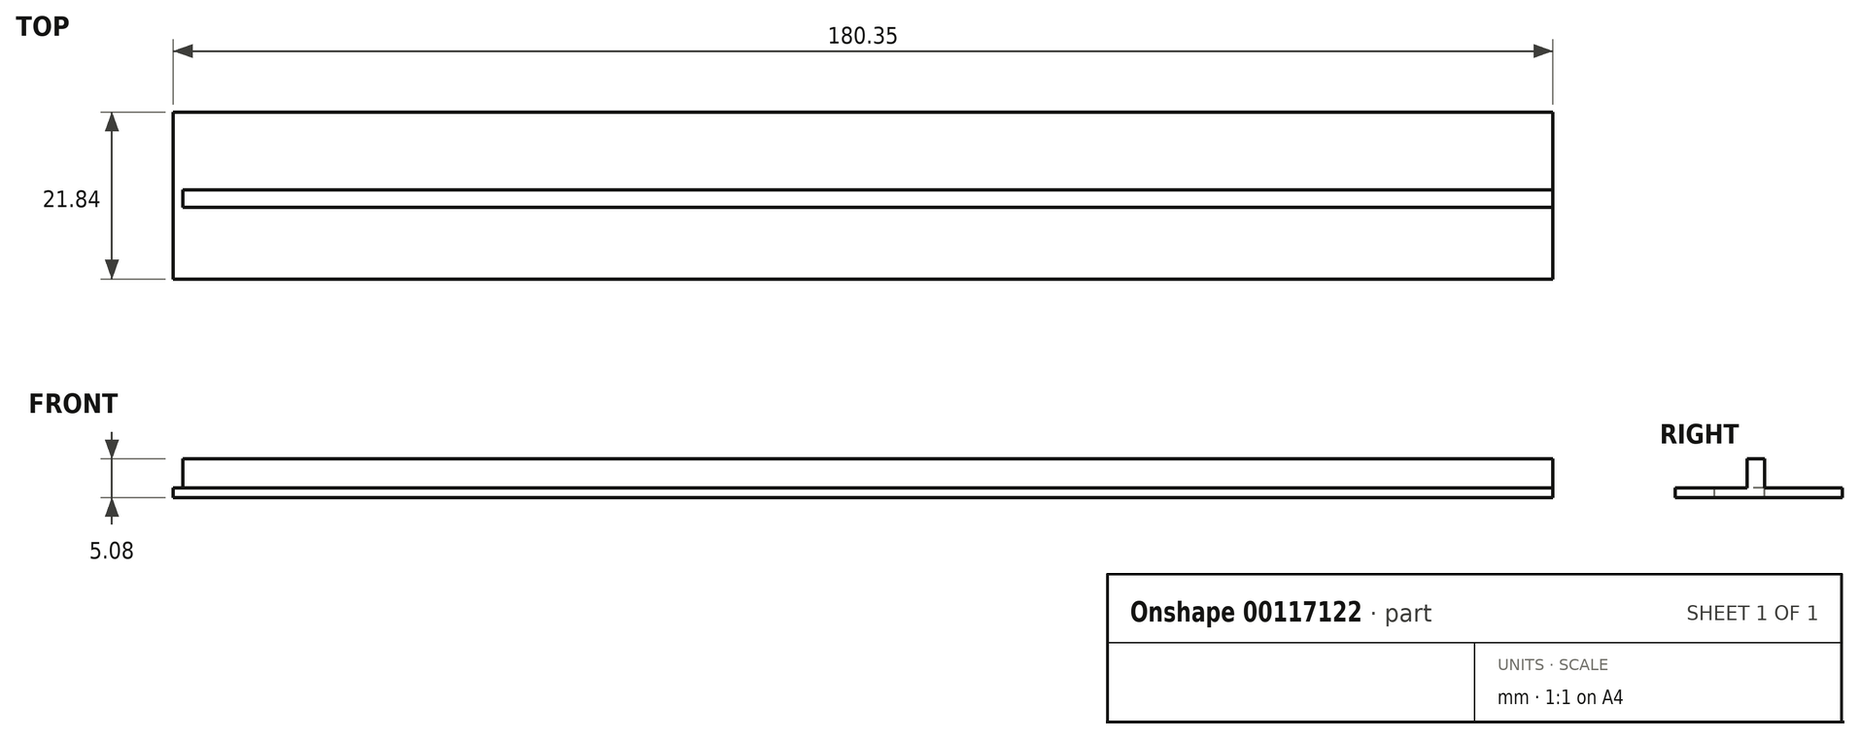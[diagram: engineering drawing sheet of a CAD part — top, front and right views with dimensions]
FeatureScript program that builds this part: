
annotation { "Feature Type Name" : "Feature", "Feature Type Description" : "" }
export const myFeature = defineFeature(function(context is Context, id is Id, definition is map)
    precondition{}
    {
        {
            var Q0;
            Q0=qCreatedBy(makeId("Front.planeOp"),FACE);
            var sketch = newSketch(context, id + "F0", { "sketchPlane" : qUnion([Q0])});
            skLineSegment(sketch, "E0.bottom", {"start": v(107.95, -50.8) * mm, "end": v(-107.95, -50.8) * mm});
            skLineSegment(sketch, "E0.top", {"start": v(107.95, 50.8) * mm, "end": v(-107.95, 50.8) * mm});
            skLineSegment(sketch, "E0.left", {"start": v(107.95, -50.8) * mm, "end": v(107.95, 50.8) * mm});
            skLineSegment(sketch, "E0.right", {"start": v(-107.95, -50.8) * mm, "end": v(-107.95, 50.8) * mm});
            skPoint(sketch, "E0.middle", {"position": v(0, 0) * mm});
            skLineSegment(sketch, "E1.bottom", {"start": v(88.9, -31.75) * mm, "end": v(-88.9, -31.75) * mm});
            skLineSegment(sketch, "E1.top", {"start": v(88.9, 31.75) * mm, "end": v(-88.9, 31.75) * mm});
            skLineSegment(sketch, "E1.left", {"start": v(88.9, -31.75) * mm, "end": v(88.9, 31.75) * mm});
            skLineSegment(sketch, "E1.right", {"start": v(-88.9, -31.75) * mm, "end": v(-88.9, 31.75) * mm});
            skSolve(sketch);
        }
        {
            var Q0;
            Q0=makeQuery(id+"F0.imprint","IMPRINT",FACE,{"disambiguationData":[TD([[makeQuery(id+"F0.imprint","IMPRINT",EDGE,{"derivedFrom":sQuery(id+"F0.wireOp",EDGE,"E0.bottom")}),-1.0]])]});
            extrude(context, id + "F1", {"entities" : qUnion([Q0]), "depth" : 12.7 * mm});
        }
        {
            var Q0;
            Q0=makeQuery(id+"F1.opExtrude","SWEPT_FACE",FACE,{"disambiguationData":[OSD([sQuery(id+"F0.wireOp",EDGE,"E0.top")])]});
            var sketch = newSketch(context, id + "F2", { "sketchPlane" : qUnion([Q0])});
            skLineSegment(sketch, "E2", {"start": v(-75.05, 0) * mm, "end": v(-80.97, -12.7) * mm});
            skLineSegment(sketch, "E3", {"start": v(-80.97, -12.7) * mm, "end": v(-78.17, -12.7) * mm});
            skLineSegment(sketch, "E4", {"start": v(-78.17, -12.7) * mm, "end": v(-72.25, 0) * mm});
            skLineSegment(sketch, "E5", {"start": v(-72.25, 0) * mm, "end": v(-75.05, 0) * mm});
            skLineSegment(sketch, "E6.1.0.0", {"start": v(-64.33, 0) * mm, "end": v(-70.25, -12.7) * mm});
            skLineSegment(sketch, "E6.1.0.1", {"start": v(-70.25, -12.7) * mm, "end": v(-67.45, -12.7) * mm});
            skLineSegment(sketch, "E6.1.0.2", {"start": v(-67.45, -12.7) * mm, "end": v(-61.53, 0) * mm});
            skLineSegment(sketch, "E6.1.0.3", {"start": v(-61.53, 0) * mm, "end": v(-64.33, 0) * mm});
            skLineSegment(sketch, "E6.2.0.0", {"start": v(-53.6, 0) * mm, "end": v(-59.53, -12.7) * mm});
            skLineSegment(sketch, "E6.2.0.1", {"start": v(-59.53, -12.7) * mm, "end": v(-56.73, -12.7) * mm});
            skLineSegment(sketch, "E6.2.0.2", {"start": v(-56.73, -12.7) * mm, "end": v(-50.8, 0) * mm});
            skLineSegment(sketch, "E6.2.0.3", {"start": v(-50.8, 0) * mm, "end": v(-53.6, 0) * mm});
            skLineSegment(sketch, "E6.3.0.0", {"start": v(-42.88, 0) * mm, "end": v(-48.8, -12.7) * mm});
            skLineSegment(sketch, "E6.3.0.1", {"start": v(-48.8, -12.7) * mm, "end": v(-46, -12.7) * mm});
            skLineSegment(sketch, "E6.3.0.2", {"start": v(-46, -12.7) * mm, "end": v(-40.08, 0) * mm});
            skLineSegment(sketch, "E6.3.0.3", {"start": v(-40.08, 0) * mm, "end": v(-42.88, 0) * mm});
            skLineSegment(sketch, "E6.4.0.0", {"start": v(-32.16, 0) * mm, "end": v(-38.08, -12.7) * mm});
            skLineSegment(sketch, "E6.4.0.1", {"start": v(-38.08, -12.7) * mm, "end": v(-35.28, -12.7) * mm});
            skLineSegment(sketch, "E6.4.0.2", {"start": v(-35.28, -12.7) * mm, "end": v(-29.36, 0) * mm});
            skLineSegment(sketch, "E6.4.0.3", {"start": v(-29.36, 0) * mm, "end": v(-32.16, 0) * mm});
            skLineSegment(sketch, "E6.5.0.0", {"start": v(-21.44, 0) * mm, "end": v(-27.36, -12.7) * mm});
            skLineSegment(sketch, "E6.5.0.1", {"start": v(-27.36, -12.7) * mm, "end": v(-24.56, -12.7) * mm});
            skLineSegment(sketch, "E6.5.0.2", {"start": v(-24.56, -12.7) * mm, "end": v(-18.64, 0) * mm});
            skLineSegment(sketch, "E6.5.0.3", {"start": v(-18.64, 0) * mm, "end": v(-21.44, 0) * mm});
            skLineSegment(sketch, "E6.6.0.0", {"start": v(-10.72, 0) * mm, "end": v(-16.64, -12.7) * mm});
            skLineSegment(sketch, "E6.6.0.1", {"start": v(-16.64, -12.7) * mm, "end": v(-13.84, -12.7) * mm});
            skLineSegment(sketch, "E6.6.0.2", {"start": v(-13.84, -12.7) * mm, "end": v(-7.92, 0) * mm});
            skLineSegment(sketch, "E6.6.0.3", {"start": v(-7.92, 0) * mm, "end": v(-10.72, 0) * mm});
            skLineSegment(sketch, "E6.direction1", {"start": v(-80.97, -12.7) * mm, "end": v(-70.25, -12.7) * mm, "construction": true});
            skLineSegment(sketch, "E7", {"start": v(75.05, 0) * mm, "end": v(80.97, -12.7) * mm});
            skLineSegment(sketch, "E8", {"start": v(80.97, -12.7) * mm, "end": v(78.17, -12.7) * mm});
            skLineSegment(sketch, "E9", {"start": v(78.17, -12.7) * mm, "end": v(72.25, 0) * mm});
            skLineSegment(sketch, "E10", {"start": v(72.25, 0) * mm, "end": v(75.05, 0) * mm});
            skLineSegment(sketch, "E11.1.0.0", {"start": v(70.25, -12.7) * mm, "end": v(67.45, -12.7) * mm});
            skLineSegment(sketch, "E11.1.0.1", {"start": v(64.33, 0) * mm, "end": v(70.25, -12.7) * mm});
            skLineSegment(sketch, "E11.1.0.2", {"start": v(61.53, 0) * mm, "end": v(64.33, 0) * mm});
            skLineSegment(sketch, "E11.1.0.3", {"start": v(67.45, -12.7) * mm, "end": v(61.53, 0) * mm});
            skLineSegment(sketch, "E11.2.0.0", {"start": v(59.53, -12.7) * mm, "end": v(56.73, -12.7) * mm});
            skLineSegment(sketch, "E11.2.0.1", {"start": v(53.6, 0) * mm, "end": v(59.53, -12.7) * mm});
            skLineSegment(sketch, "E11.2.0.2", {"start": v(50.8, 0) * mm, "end": v(53.6, 0) * mm});
            skLineSegment(sketch, "E11.2.0.3", {"start": v(56.73, -12.7) * mm, "end": v(50.8, 0) * mm});
            skLineSegment(sketch, "E11.3.0.0", {"start": v(48.8, -12.7) * mm, "end": v(46, -12.7) * mm});
            skLineSegment(sketch, "E11.3.0.1", {"start": v(42.88, 0) * mm, "end": v(48.8, -12.7) * mm});
            skLineSegment(sketch, "E11.3.0.2", {"start": v(40.08, 0) * mm, "end": v(42.88, 0) * mm});
            skLineSegment(sketch, "E11.3.0.3", {"start": v(46, -12.7) * mm, "end": v(40.08, 0) * mm});
            skLineSegment(sketch, "E11.4.0.0", {"start": v(38.08, -12.7) * mm, "end": v(35.28, -12.7) * mm});
            skLineSegment(sketch, "E11.4.0.1", {"start": v(32.16, 0) * mm, "end": v(38.08, -12.7) * mm});
            skLineSegment(sketch, "E11.4.0.2", {"start": v(29.36, 0) * mm, "end": v(32.16, 0) * mm});
            skLineSegment(sketch, "E11.4.0.3", {"start": v(35.28, -12.7) * mm, "end": v(29.36, 0) * mm});
            skLineSegment(sketch, "E11.5.0.0", {"start": v(27.36, -12.7) * mm, "end": v(24.56, -12.7) * mm});
            skLineSegment(sketch, "E11.5.0.1", {"start": v(21.44, 0) * mm, "end": v(27.36, -12.7) * mm});
            skLineSegment(sketch, "E11.5.0.2", {"start": v(18.64, 0) * mm, "end": v(21.44, 0) * mm});
            skLineSegment(sketch, "E11.5.0.3", {"start": v(24.56, -12.7) * mm, "end": v(18.64, 0) * mm});
            skLineSegment(sketch, "E11.6.0.0", {"start": v(16.64, -12.7) * mm, "end": v(13.84, -12.7) * mm});
            skLineSegment(sketch, "E11.6.0.1", {"start": v(10.72, 0) * mm, "end": v(16.64, -12.7) * mm});
            skLineSegment(sketch, "E11.6.0.2", {"start": v(7.92, 0) * mm, "end": v(10.72, 0) * mm});
            skLineSegment(sketch, "E11.6.0.3", {"start": v(13.84, -12.7) * mm, "end": v(7.92, 0) * mm});
            skLineSegment(sketch, "E11.direction1", {"start": v(78.17, -12.7) * mm, "end": v(67.45, -12.7) * mm, "construction": true});
            skLineSegment(sketch, "E12", {"start": v(0, 0) * mm, "end": v(0, -12.7) * mm, "construction": true});
            skLineSegment(sketch, "E13", {"start": v(0, 0) * mm, "end": v(-5.92, -12.7) * mm});
            skLineSegment(sketch, "E14", {"start": v(0, 0) * mm, "end": v(5.92, -12.7) * mm});
            skLineSegment(sketch, "E15", {"start": v(-5.92, -12.7) * mm, "end": v(5.92, -12.7) * mm});
            skSolve(sketch);
        }
        {
            var Q0;
            Q0=qSketchRegion(id+"F2",true);
            extrude(context, id + "F3", {"entities" : qUnion([Q0]), "operationType" : NewBodyOperationType.ADD, "oppositeDirection" : true, "depth" : 101.6 * mm});
        }
        {
            var Q0;
            Q0=makeQuery(id+"F1.opExtrude","CAP_EDGE",EDGE,{"disambiguationData":[OSD([sQuery(id+"F0.wireOp",EDGE,"E0.top")])],"isStart":false});
            var Q1;
            Q1=makeQuery(id+"F1.opExtrude","CAP_EDGE",EDGE,{"disambiguationData":[OSD([sQuery(id+"F0.wireOp",EDGE,"E0.right")])],"isStart":false});
            var Q2;
            Q2=makeQuery(id+"F1.opExtrude","CAP_EDGE",EDGE,{"disambiguationData":[OSD([sQuery(id+"F0.wireOp",EDGE,"E0.bottom")])],"isStart":false});
            var Q3;
            Q3=makeQuery(id+"F1.opExtrude","CAP_EDGE",EDGE,{"disambiguationData":[OSD([sQuery(id+"F0.wireOp",EDGE,"E0.left")])],"isStart":false});
            fillet(context, id + "F4", {"entities" : qUnion([Q0, Q1, Q2, Q3]), "radius" : 12.7 * mm, "tangentPropagation" : true, "allowEdgeOverflow" : false});
        }
        {
            var Q0;
            Q0=makeQuery(id+"F3.boolean.opBoolean","MERGE",FACE,{"derivedFrom":[makeQuery(id+"F1.opExtrude","CAP_FACE",FACE,{"disambiguationData":[OSD([sQuery(id+"F0.wireOp",EDGE,"E0.bottom"),sQuery(id+"F0.wireOp",EDGE,"E0.top"),sQuery(id+"F0.wireOp",EDGE,"E0.left"),sQuery(id+"F0.wireOp",EDGE,"E0.right"),sQuery(id+"F0.wireOp",EDGE,"E1.bottom"),sQuery(id+"F0.wireOp",EDGE,"E1.top"),sQuery(id+"F0.wireOp",EDGE,"E1.left"),sQuery(id+"F0.wireOp",EDGE,"E1.right")])],"isStart":true}),makeQuery(id+"F3.opExtrude","SWEPT_FACE",FACE,{"disambiguationData":[OSD([sQuery(id+"F2.wireOp",EDGE,"E5")])]}),makeQuery(id+"F3.opExtrude","SWEPT_FACE",FACE,{"disambiguationData":[OSD([sQuery(id+"F2.wireOp",EDGE,"E6.1.0.3")])]}),makeQuery(id+"F3.opExtrude","SWEPT_FACE",FACE,{"disambiguationData":[OSD([sQuery(id+"F2.wireOp",EDGE,"E6.2.0.3")])]}),makeQuery(id+"F3.opExtrude","SWEPT_FACE",FACE,{"disambiguationData":[OSD([sQuery(id+"F2.wireOp",EDGE,"E6.3.0.3")])]}),makeQuery(id+"F3.opExtrude","SWEPT_FACE",FACE,{"disambiguationData":[OSD([sQuery(id+"F2.wireOp",EDGE,"E6.4.0.3")])]}),makeQuery(id+"F3.opExtrude","SWEPT_FACE",FACE,{"disambiguationData":[OSD([sQuery(id+"F2.wireOp",EDGE,"E6.5.0.3")])]}),makeQuery(id+"F3.opExtrude","SWEPT_FACE",FACE,{"disambiguationData":[OSD([sQuery(id+"F2.wireOp",EDGE,"E6.6.0.3")])]}),makeQuery(id+"F3.opExtrude","SWEPT_FACE",FACE,{"disambiguationData":[OSD([sQuery(id+"F2.wireOp",EDGE,"E10")])]}),makeQuery(id+"F3.opExtrude","SWEPT_FACE",FACE,{"disambiguationData":[OSD([sQuery(id+"F2.wireOp",EDGE,"E11.1.0.2")])]}),makeQuery(id+"F3.opExtrude","SWEPT_FACE",FACE,{"disambiguationData":[OSD([sQuery(id+"F2.wireOp",EDGE,"E11.2.0.2")])]}),makeQuery(id+"F3.opExtrude","SWEPT_FACE",FACE,{"disambiguationData":[OSD([sQuery(id+"F2.wireOp",EDGE,"E11.3.0.2")])]}),makeQuery(id+"F3.opExtrude","SWEPT_FACE",FACE,{"disambiguationData":[OSD([sQuery(id+"F2.wireOp",EDGE,"E11.4.0.2")])]}),makeQuery(id+"F3.opExtrude","SWEPT_FACE",FACE,{"disambiguationData":[OSD([sQuery(id+"F2.wireOp",EDGE,"E11.5.0.2")])]}),makeQuery(id+"F3.opExtrude","SWEPT_FACE",FACE,{"disambiguationData":[OSD([sQuery(id+"F2.wireOp",EDGE,"E11.6.0.2")])]})]});
            var sketch = newSketch(context, id + "F5", { "sketchPlane" : qUnion([Q0])});
            skLineSegment(sketch, "E16.bottom", {"start": v(90.17, -33.02) * mm, "end": v(-90.17, -33.02) * mm});
            skLineSegment(sketch, "E16.top", {"start": v(90.17, 33.02) * mm, "end": v(-90.17, 33.02) * mm});
            skLineSegment(sketch, "E16.right", {"start": v(-90.17, -33.02) * mm, "end": v(-90.17, 33.02) * mm});
            skPoint(sketch, "E16.middle", {"position": v(0, 0) * mm});
            skLineSegment(sketch, "E17.bottom", {"start": v(88.9, -31.75) * mm, "end": v(-88.9, -31.75) * mm});
            skLineSegment(sketch, "E17.top", {"start": v(88.9, 31.75) * mm, "end": v(-88.9, 31.75) * mm});
            skLineSegment(sketch, "E17.right", {"start": v(-88.9, -31.75) * mm, "end": v(-88.9, 31.75) * mm});
            skLineSegment(sketch, "E18", {"start": v(88.9, 31.75) * mm, "end": v(90.17, 31.75) * mm});
            skLineSegment(sketch, "E19", {"start": v(90.17, 31.75) * mm, "end": v(90.17, 33.02) * mm});
            skLineSegment(sketch, "E20", {"start": v(88.9, -31.75) * mm, "end": v(90.17, -31.75) * mm});
            skLineSegment(sketch, "E21", {"start": v(90.17, -31.75) * mm, "end": v(90.17, -33.02) * mm});
            skSolve(sketch);
        }
        {
            var Q0;
            Q0=qSketchRegion(id+"F5",true);
            extrude(context, id + "F6", {"entities" : qUnion([Q0]), "operationType" : NewBodyOperationType.ADD, "depth" : 3.3 * mm});
        }
        {
            var Q0;
            Q0=makeQuery(id+"F6.opExtrude","CAP_FACE",FACE,{"disambiguationData":[OSD([sQuery(id+"F5.wireOp",EDGE,"E16.bottom"),sQuery(id+"F5.wireOp",EDGE,"E16.top"),sQuery(id+"F5.wireOp",EDGE,"E16.right"),sQuery(id+"F5.wireOp",EDGE,"E17.bottom"),sQuery(id+"F5.wireOp",EDGE,"E17.top"),sQuery(id+"F5.wireOp",EDGE,"E17.right"),sQuery(id+"F5.wireOp",EDGE,"E18"),sQuery(id+"F5.wireOp",EDGE,"E19"),sQuery(id+"F5.wireOp",EDGE,"E20"),sQuery(id+"F5.wireOp",EDGE,"E21")])],"isStart":false});
            var sketch = newSketch(context, id + "F7", { "sketchPlane" : qUnion([Q0])});
            skLineSegment(sketch, "E22.bottom", {"start": v(-90.17, 33.02) * mm, "end": v(88.9, 33.02) * mm});
            skLineSegment(sketch, "E22.top", {"start": v(-90.17, -33.02) * mm, "end": v(88.9, -33.02) * mm});
            skLineSegment(sketch, "E22.left", {"start": v(-90.17, 33.02) * mm, "end": v(-90.17, -33.02) * mm});
            skLineSegment(sketch, "E22.right", {"start": v(88.9, 33.02) * mm, "end": v(88.9, -33.02) * mm});
            skLineSegment(sketch, "E23.bottom", {"start": v(-86.36, 27.94) * mm, "end": v(86.36, 27.94) * mm});
            skLineSegment(sketch, "E23.top", {"start": v(-86.36, -27.94) * mm, "end": v(86.36, -27.94) * mm});
            skLineSegment(sketch, "E23.left", {"start": v(-86.36, 27.94) * mm, "end": v(-86.36, -27.94) * mm});
            skLineSegment(sketch, "E23.right", {"start": v(86.36, 27.94) * mm, "end": v(86.36, -27.94) * mm});
            skSolve(sketch);
        }
        {
            var Q0;
            Q0=qSketchRegion(id+"F7",true);
            extrude(context, id + "F8", {"entities" : qUnion([Q0]), "operationType" : NewBodyOperationType.ADD, "depth" : 1.78 * mm});
        }
        {
            var Q0;
            Q0=makeQuery(id+"F8.opExtrude","CAP_FACE",FACE,{"disambiguationData":[OSD([sQuery(id+"F7.wireOp",EDGE,"E22.bottom"),sQuery(id+"F7.wireOp",EDGE,"E22.top"),sQuery(id+"F7.wireOp",EDGE,"E22.left"),sQuery(id+"F7.wireOp",EDGE,"E22.right"),sQuery(id+"F7.wireOp",EDGE,"E23.bottom"),sQuery(id+"F7.wireOp",EDGE,"E23.top"),sQuery(id+"F7.wireOp",EDGE,"E23.left"),sQuery(id+"F7.wireOp",EDGE,"E23.right")])],"isStart":false});
            var sketch = newSketch(context, id + "F9", { "sketchPlane" : qUnion([Q0])});
            skLineSegment(sketch, "E24.bottom", {"start": v(-90.17, 33.02) * mm, "end": v(88.9, 33.02) * mm});
            skLineSegment(sketch, "E24.top", {"start": v(-90.17, -33.02) * mm, "end": v(88.9, -33.02) * mm});
            skLineSegment(sketch, "E24.left", {"start": v(-90.17, 33.02) * mm, "end": v(-90.17, -33.02) * mm});
            skLineSegment(sketch, "E25.bottom", {"start": v(-88.9, 31.75) * mm, "end": v(87.63, 31.75) * mm});
            skLineSegment(sketch, "E25.top", {"start": v(-88.9, -31.75) * mm, "end": v(87.63, -31.75) * mm});
            skLineSegment(sketch, "E25.left", {"start": v(-88.9, 31.75) * mm, "end": v(-88.9, -31.75) * mm});
            skLineSegment(sketch, "E26", {"start": v(88.9, -33.02) * mm, "end": v(90.18, -33.02) * mm});
            skLineSegment(sketch, "E27", {"start": v(90.18, -33.02) * mm, "end": v(90.18, -31.75) * mm});
            skLineSegment(sketch, "E28", {"start": v(90.18, -31.75) * mm, "end": v(87.63, -31.75) * mm});
            skLineSegment(sketch, "E29", {"start": v(88.9, 33.02) * mm, "end": v(90.17, 33.02) * mm});
            skLineSegment(sketch, "E30", {"start": v(90.17, 33.02) * mm, "end": v(90.17, 31.75) * mm});
            skLineSegment(sketch, "E31", {"start": v(90.17, 31.75) * mm, "end": v(87.63, 31.75) * mm});
            skSolve(sketch);
        }
        {
            var Q0;
            {var subQ5=sQuery(id+"F9.wireOp",EDGE,"E24.bottom");Q0=makeQuery(id+"F9.imprint","IMPRINT",FACE,{"disambiguationData":[TD([[makeQuery(id+"F9.imprint","IMPRINT",EDGE,{"derivedFrom":subQ5}),1.0]])]});}
            var Q1;
            {var subQ0=sQuery(id+"F9.wireOp",EDGE,"E29");Q1=makeQuery(id+"F9.imprint","IMPRINT",FACE,{"disambiguationData":[TD([[makeQuery(id+"F9.imprint","IMPRINT",EDGE,{"derivedFrom":subQ0}),-1.0]])]});}
            var Q2;
            {var subQ0=sQuery(id+"F9.wireOp",EDGE,"E26");Q2=makeQuery(id+"F9.imprint","IMPRINT",FACE,{"disambiguationData":[TD([[makeQuery(id+"F9.imprint","IMPRINT",EDGE,{"derivedFrom":subQ0}),1.0]])]});}
            extrude(context, id + "F10", {"entities" : qUnion([Q0, Q1, Q2]), "operationType" : NewBodyOperationType.ADD, "depth" : 4.32 * mm});
        }
        {
            var Q0;
            {var subQ0=sQuery(id+"F5.wireOp",EDGE,"E21");var subQ1=sQuery(id+"F5.wireOp",EDGE,"E20");var subQ2=sQuery(id+"F5.wireOp",EDGE,"E17.bottom");var subQ3=sQuery(id+"F5.wireOp",EDGE,"E16.bottom");Q0=makeQuery(id+"F8.boolean.opBoolean","SPLIT",FACE,{"disambiguationData":[TD([makeQuery(id+"F1.opExtrude","SWEPT_FACE",FACE,{"disambiguationData":[OSD([sQuery(id+"F0.wireOp",EDGE,"E1.bottom")])]})])],"derivedFrom":makeQuery(id+"F6.opExtrude","CAP_FACE",FACE,{"disambiguationData":[OSD([subQ3,sQuery(id+"F5.wireOp",EDGE,"E16.top"),sQuery(id+"F5.wireOp",EDGE,"E16.right"),subQ2,sQuery(id+"F5.wireOp",EDGE,"E17.top"),sQuery(id+"F5.wireOp",EDGE,"E17.right"),sQuery(id+"F5.wireOp",EDGE,"E18"),sQuery(id+"F5.wireOp",EDGE,"E19"),subQ1,subQ0])],"isStart":false})});}
            var sketch = newSketch(context, id + "F11", { "sketchPlane" : qUnion([Q0])});
            skLineSegment(sketch, "E32.bottom", {"start": v(88.9, -33.02) * mm, "end": v(90.17, -33.02) * mm});
            skLineSegment(sketch, "E32.top", {"start": v(88.9, -31.75) * mm, "end": v(90.17, -31.75) * mm});
            skLineSegment(sketch, "E32.left", {"start": v(88.9, -33.02) * mm, "end": v(88.9, -31.75) * mm});
            skLineSegment(sketch, "E32.right", {"start": v(90.17, -33.02) * mm, "end": v(90.17, -31.75) * mm});
            skSolve(sketch);
        }
        {
            var Q0;
            Q0=qSketchRegion(id+"F11",true);
            extrude(context, id + "F12", {"entities" : qUnion([Q0]), "operationType" : NewBodyOperationType.ADD, "depth" : 1.78 * mm});
        }
        {
            var Q0;
            Q0=makeQuery(id+"F10.opExtrude","CAP_FACE",FACE,{"disambiguationData":[OSD([sQuery(id+"F9.wireOp",EDGE,"E24.bottom"),sQuery(id+"F9.wireOp",EDGE,"E24.top"),sQuery(id+"F9.wireOp",EDGE,"E24.left"),sQuery(id+"F9.wireOp",EDGE,"E25.bottom"),sQuery(id+"F9.wireOp",EDGE,"E25.top"),sQuery(id+"F9.wireOp",EDGE,"E25.left"),sQuery(id+"F9.wireOp",EDGE,"E26"),sQuery(id+"F9.wireOp",EDGE,"E27"),sQuery(id+"F9.wireOp",EDGE,"E28"),sQuery(id+"F9.wireOp",EDGE,"E29"),sQuery(id+"F9.wireOp",EDGE,"E30"),sQuery(id+"F9.wireOp",EDGE,"E31")])],"isStart":false});
            var sketch = newSketch(context, id + "F13", { "sketchPlane" : qUnion([Q0])});
            skLineSegment(sketch, "E33.bottom", {"start": v(-90.17, 33.02) * mm, "end": v(88.9, 33.02) * mm});
            skLineSegment(sketch, "E33.top", {"start": v(-90.17, -33.02) * mm, "end": v(88.9, -33.02) * mm});
            skLineSegment(sketch, "E34.bottom", {"start": v(-84.84, 27.94) * mm, "end": v(88.9, 27.94) * mm});
            skLineSegment(sketch, "E34.top", {"start": v(-84.84, -27.94) * mm, "end": v(88.9, -27.94) * mm});
            skLineSegment(sketch, "E35", {"start": v(-84.84, 27.94) * mm, "end": v(-90.17, 27.94) * mm});
            skLineSegment(sketch, "E36", {"start": v(-90.17, 27.94) * mm, "end": v(-90.17, 33.02) * mm});
            skLineSegment(sketch, "E37", {"start": v(-84.84, -27.94) * mm, "end": v(-90.17, -27.94) * mm});
            skLineSegment(sketch, "E38", {"start": v(-90.17, -27.94) * mm, "end": v(-90.17, -33.02) * mm});
            skLineSegment(sketch, "E39.bottom", {"start": v(-90.17, 27.94) * mm, "end": v(-88.9, 27.94) * mm});
            skLineSegment(sketch, "E39.top", {"start": v(-90.17, -27.94) * mm, "end": v(-88.9, -27.94) * mm});
            skLineSegment(sketch, "E39.left", {"start": v(-90.17, 27.94) * mm, "end": v(-90.17, -27.94) * mm});
            skLineSegment(sketch, "E39.right", {"start": v(-88.9, 27.94) * mm, "end": v(-88.9, -27.94) * mm});
            skLineSegment(sketch, "E40", {"start": v(88.9, -27.94) * mm, "end": v(88.9, -33.02) * mm});
            skLineSegment(sketch, "E41", {"start": v(88.9, 27.94) * mm, "end": v(88.9, 33.02) * mm});
            skSolve(sketch);
        }
        {
            var Q0;
            Q0=qSketchRegion(id+"F13",true);
            extrude(context, id + "F14", {"entities" : qUnion([Q0]), "operationType" : NewBodyOperationType.ADD, "depth" : 2.3 * mm});
        }
        {
            var Q0;
            Q0=makeQuery(id+"F14.opExtrude","SWEPT_FACE",FACE,{"disambiguationData":[OSD([sQuery(id+"F13.wireOp",EDGE,"E34.top"),sQuery(id+"F13.wireOp",EDGE,"E37"),sQuery(id+"F13.wireOp",EDGE,"TGxW7JvE-hO0u-tt39-ioUT-bYuH0o1wrKsi")])]});
            var sketch = newSketch(context, id + "F15", { "sketchPlane" : qUnion([Q0])});
            skSolve(sketch);
        }
        {
            var Q0;
            Q0=makeQuery(id+"Fv8F5Soem3vfvmW_1.boolean.opBoolean","MERGE",FACE,{"derivedFrom":[makeQuery(id+"F14.opExtrude","CAP_FACE",FACE,{"disambiguationData":[OSD([sQuery(id+"F13.wireOp",EDGE,"E33.bottom"),sQuery(id+"F13.wireOp",EDGE,"E33.top"),sQuery(id+"F13.wireOp",EDGE,"E34.bottom"),sQuery(id+"F13.wireOp",EDGE,"E34.top"),sQuery(id+"F13.wireOp",EDGE,"E35"),sQuery(id+"F13.wireOp",EDGE,"E36"),sQuery(id+"F13.wireOp",EDGE,"E37"),sQuery(id+"F13.wireOp",EDGE,"E38"),sQuery(id+"F13.wireOp",EDGE,"E39.left"),sQuery(id+"F13.wireOp",EDGE,"E39.right"),sQuery(id+"F13.wireOp",EDGE,"TGxW7JvE-hO0u-tt39-ioUT-bYuH0o1wrKsi"),sQuery(id+"F13.wireOp",EDGE,"xJwFBrmR-DKHQ-Ms6E-cGLF-1sDl0en4KIHk"),sQuery(id+"F13.wireOp",EDGE,"KjPjYPhn-M9NA-BWyU-6eae-7lh8KEkwCyoe"),sQuery(id+"F13.wireOp",EDGE,"DDPbrne3-7nOW-QVff-d2O1-u6GeuogKL0BI")])],"isStart":false}),makeQuery(id+"Fv8F5Soem3vfvmW_1.opExtrude","SWEPT_FACE",FACE,{"disambiguationData":[OSD([sQuery(id+"F15.wireOp",EDGE,"I5fvG48v-rP8C-mtnB-2jEv-sWBCkAZKz6mY.bottom")])]})]});
            var sketch = newSketch(context, id + "F16", { "sketchPlane" : qUnion([Q0])});
            skLineSegment(sketch, "E42.bottom", {"start": v(-90.17, 33.02) * mm, "end": v(90.17, 33.02) * mm});
            skLineSegment(sketch, "E42.top", {"start": v(-90.17, -33.02) * mm, "end": v(90.17, -33.02) * mm});
            skLineSegment(sketch, "E42.left", {"start": v(-90.17, 33.02) * mm, "end": v(-90.17, -33.02) * mm});
            skLineSegment(sketch, "E43.bottom", {"start": v(-88.9, 31.75) * mm, "end": v(84.62, 31.75) * mm});
            skLineSegment(sketch, "E43.top", {"start": v(-88.9, -31.75) * mm, "end": v(84.62, -31.75) * mm});
            skLineSegment(sketch, "E43.left", {"start": v(-88.9, 31.75) * mm, "end": v(-88.9, -31.75) * mm});
            skLineSegment(sketch, "E44", {"start": v(84.62, 31.75) * mm, "end": v(90.17, 31.75) * mm});
            skLineSegment(sketch, "E45", {"start": v(90.17, 33.02) * mm, "end": v(90.17, 31.75) * mm});
            skLineSegment(sketch, "E46", {"start": v(84.62, -31.75) * mm, "end": v(90.17, -31.75) * mm});
            skLineSegment(sketch, "E47", {"start": v(90.17, -33.02) * mm, "end": v(90.17, -31.75) * mm});
            skSolve(sketch);
        }
        {
            var Q0;
            Q0=qSketchRegion(id+"F16",true);
            extrude(context, id + "F17", {"entities" : qUnion([Q0]), "operationType" : NewBodyOperationType.ADD, "depth" : 10.16 * mm});
        }
        {
            var Q0;
            {var subQ0=sQuery(id+"F5.wireOp",EDGE,"E18");var subQ1=sQuery(id+"F5.wireOp",EDGE,"E17.top");var subQ2=sQuery(id+"F5.wireOp",EDGE,"E19");var subQ3=sQuery(id+"F5.wireOp",EDGE,"E16.top");Q0=makeQuery(id+"F8.boolean.opBoolean","SPLIT",FACE,{"disambiguationData":[TD([makeQuery(id+"F1.opExtrude","SWEPT_FACE",FACE,{"disambiguationData":[OSD([sQuery(id+"F0.wireOp",EDGE,"E1.top")])]})])],"derivedFrom":makeQuery(id+"F6.opExtrude","CAP_FACE",FACE,{"disambiguationData":[OSD([sQuery(id+"F5.wireOp",EDGE,"E16.bottom"),subQ3,sQuery(id+"F5.wireOp",EDGE,"E16.right"),sQuery(id+"F5.wireOp",EDGE,"E17.bottom"),subQ1,sQuery(id+"F5.wireOp",EDGE,"E17.right"),subQ0,subQ2,sQuery(id+"F5.wireOp",EDGE,"E20"),sQuery(id+"F5.wireOp",EDGE,"E21")])],"isStart":false})});}
            var sketch = newSketch(context, id + "F18", { "sketchPlane" : qUnion([Q0])});
            skLineSegment(sketch, "E48.bottom", {"start": v(88.9, 33.02) * mm, "end": v(90.17, 33.02) * mm});
            skLineSegment(sketch, "E48.top", {"start": v(88.9, 31.75) * mm, "end": v(90.17, 31.75) * mm});
            skLineSegment(sketch, "E48.left", {"start": v(88.9, 33.02) * mm, "end": v(88.9, 31.75) * mm});
            skLineSegment(sketch, "E48.right", {"start": v(90.17, 33.02) * mm, "end": v(90.17, 31.75) * mm});
            skSolve(sketch);
        }
        {
            var Q0;
            Q0=qSketchRegion(id+"F18",true);
            extrude(context, id + "F19", {"entities" : qUnion([Q0]), "operationType" : NewBodyOperationType.ADD, "depth" : 1.78 * mm});
        }
        {
            var Q0;
            {var subQ0=sQuery(id+"F9.wireOp",EDGE,"E27");var subQ1=sQuery(id+"F9.wireOp",EDGE,"E26");var subQ2=sQuery(id+"F9.wireOp",EDGE,"E24.top");var subQ4=sQuery(id+"F9.wireOp",EDGE,"E28");Q0=makeQuery(id+"F14.boolean.opBoolean","SPLIT",FACE,{"disambiguationData":[TD([makeQuery(id+"F6.opExtrude","SWEPT_FACE",FACE,{"disambiguationData":[OSD([sQuery(id+"F5.wireOp",EDGE,"E16.bottom")])]})])],"derivedFrom":makeQuery(id+"F10.opExtrude","CAP_FACE",FACE,{"disambiguationData":[OSD([sQuery(id+"F9.wireOp",EDGE,"E24.bottom"),subQ2,sQuery(id+"F9.wireOp",EDGE,"E24.left"),sQuery(id+"F9.wireOp",EDGE,"E25.bottom"),sQuery(id+"F9.wireOp",EDGE,"E25.top"),sQuery(id+"F9.wireOp",EDGE,"E25.left"),subQ1,subQ0,subQ4,sQuery(id+"F9.wireOp",EDGE,"E29"),sQuery(id+"F9.wireOp",EDGE,"E30"),sQuery(id+"F9.wireOp",EDGE,"E31")])],"isStart":false})});}
            var sketch = newSketch(context, id + "F20", { "sketchPlane" : qUnion([Q0])});
            skLineSegment(sketch, "E49.bottom", {"start": v(88.9, -33.02) * mm, "end": v(90.18, -33.02) * mm});
            skLineSegment(sketch, "E49.top", {"start": v(88.9, -31.75) * mm, "end": v(90.18, -31.75) * mm});
            skLineSegment(sketch, "E49.left", {"start": v(88.9, -33.02) * mm, "end": v(88.9, -31.75) * mm});
            skLineSegment(sketch, "E49.right", {"start": v(90.18, -33.02) * mm, "end": v(90.18, -31.75) * mm});
            skSolve(sketch);
        }
        {
            var Q0;
            {var subQ2=sQuery(id+"F9.wireOp",EDGE,"E30");var subQ3=sQuery(id+"F9.wireOp",EDGE,"E29");var subQ4=sQuery(id+"F9.wireOp",EDGE,"E24.bottom");var subQ5=sQuery(id+"F9.wireOp",EDGE,"E31");Q0=makeQuery(id+"F14.boolean.opBoolean","SPLIT",FACE,{"disambiguationData":[TD([makeQuery(id+"F6.opExtrude","SWEPT_FACE",FACE,{"disambiguationData":[OSD([sQuery(id+"F5.wireOp",EDGE,"E16.top")])]})])],"derivedFrom":makeQuery(id+"F10.opExtrude","CAP_FACE",FACE,{"disambiguationData":[OSD([subQ4,sQuery(id+"F9.wireOp",EDGE,"E24.top"),sQuery(id+"F9.wireOp",EDGE,"E24.left"),sQuery(id+"F9.wireOp",EDGE,"E25.bottom"),sQuery(id+"F9.wireOp",EDGE,"E25.top"),sQuery(id+"F9.wireOp",EDGE,"E25.left"),sQuery(id+"F9.wireOp",EDGE,"E26"),sQuery(id+"F9.wireOp",EDGE,"E27"),sQuery(id+"F9.wireOp",EDGE,"E28"),subQ3,subQ2,subQ5])],"isStart":false})});}
            var sketch = newSketch(context, id + "F21", { "sketchPlane" : qUnion([Q0])});
            skLineSegment(sketch, "E50.bottom", {"start": v(88.9, 31.75) * mm, "end": v(90.17, 31.75) * mm});
            skLineSegment(sketch, "E50.top", {"start": v(88.9, 33.02) * mm, "end": v(90.17, 33.02) * mm});
            skLineSegment(sketch, "E50.left", {"start": v(88.9, 31.75) * mm, "end": v(88.9, 33.02) * mm});
            skLineSegment(sketch, "E50.right", {"start": v(90.17, 31.75) * mm, "end": v(90.17, 33.02) * mm});
            skSolve(sketch);
        }
        {
            var Q0;
            Q0=qSketchRegion(id+"F21",true);
            var Q1;
            Q1=qSketchRegion(id+"F20",true);
            extrude(context, id + "F22", {"entities" : qUnion([Q0, Q1]), "operationType" : NewBodyOperationType.ADD, "depth" : 2.3 * mm});
        }
        {
            var Q0;
            Q0=makeQuery(id+"F12.boolean.opBoolean","MERGE",FACE,{"derivedFrom":[makeQuery(id+"F6.opExtrude","SWEPT_FACE",FACE,{"disambiguationData":[OSD([sQuery(id+"F5.wireOp",EDGE,"E21")])]}),makeQuery(id+"F12.opExtrude","SWEPT_FACE",FACE,{"disambiguationData":[OSD([sQuery(id+"F11.wireOp",EDGE,"E32.right")])]})]});
            var sketch = newSketch(context, id + "F23", { "sketchPlane" : qUnion([Q0])});
            skLineSegment(sketch, "E51.0.6", {"start": v(-21.84, 31.75) * mm, "end": v(-21.84, -31.75) * mm});
            skLineSegment(sketch, "E51.0.7", {"start": v(-21.84, -31.75) * mm, "end": v(-11.68, -31.75) * mm});
            skLineSegment(sketch, "E51.0.8", {"start": v(-11.68, -31.75) * mm, "end": v(-11.68, -27.94) * mm});
            skLineSegment(sketch, "E51.0.9", {"start": v(-11.68, -27.94) * mm, "end": v(-9.4, -27.94) * mm});
            skLineSegment(sketch, "E51.0.10", {"start": v(-9.4, -27.94) * mm, "end": v(-9.4, -31.75) * mm});
            skLineSegment(sketch, "E51.0.11", {"start": v(-9.4, -31.75) * mm, "end": v(-5.08, -31.75) * mm});
            skLineSegment(sketch, "E52.0.2", {"start": v(-21.84, 33.02) * mm, "end": v(-21.84, 31.75) * mm});
            skLineSegment(sketch, "E53.0.0", {"start": v(0, 31.75) * mm, "end": v(0, 33.02) * mm});
            skLineSegment(sketch, "E54.0.2", {"start": v(-5.08, -31.75) * mm, "end": v(-3.3, -31.75) * mm});
            skLineSegment(sketch, "E55.0", {"start": v(0, -50.8) * mm, "end": v(0, 50.8) * mm});
            skLineSegment(sketch, "E56", {"start": v(0, -50.8) * mm, "end": v(15.56, -50.8) * mm});
            skLineSegment(sketch, "E57", {"start": v(15.56, -50.8) * mm, "end": v(15.56, 54.86) * mm});
            skLineSegment(sketch, "E58", {"start": v(15.56, 54.86) * mm, "end": v(0, 50.8) * mm});
            skLineSegment(sketch, "E59.bottom", {"start": v(-21.84, 36.42) * mm, "end": v(0, 36.42) * mm});
            skLineSegment(sketch, "E59.top", {"start": v(-21.84, -31.75) * mm, "end": v(0, -31.75) * mm});
            skLineSegment(sketch, "E59.left", {"start": v(-21.84, 36.42) * mm, "end": v(-21.84, -31.75) * mm});
            skLineSegment(sketch, "E59.right", {"start": v(0, 36.42) * mm, "end": v(0, -31.75) * mm});
            skSolve(sketch);
        }
        {
            var Q0;
            {var subQ6=sQuery(id+"F23.wireOp",EDGE,"E56");Q0=makeQuery(id+"F23.imprint","IMPRINT",FACE,{"disambiguationData":[TD([[makeQuery(id+"F23.imprint","IMPRINT",EDGE,{"derivedFrom":subQ6}),1.0]])]});}
            var Q1;
            {var subQ9=sQuery(id+"F23.wireOp",EDGE,"E51.0.8");Q1=makeQuery(id+"F23.imprint","IMPRINT",FACE,{"disambiguationData":[TD([[makeQuery(id+"F23.imprint","IMPRINT",EDGE,{"derivedFrom":subQ9}),1.0]])]});}
            extrude(context, id + "F24", {"entities" : qUnion([Q0, Q1]), "operationType" : NewBodyOperationType.REMOVE, "endBound" : BoundingType.THROUGH_ALL, "oppositeDirection" : true, "depth" : 25.4 * mm, "hasSecondDirection" : true, "secondDirectionBound" : BoundingType.THROUGH_ALL, "secondDirectionOppositeDirection" : false, "secondDirectionDepth" : 25.4 * mm});
        }
    });
